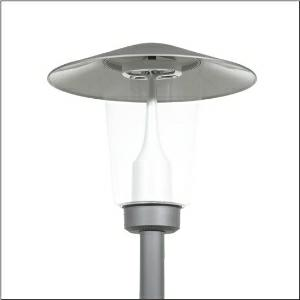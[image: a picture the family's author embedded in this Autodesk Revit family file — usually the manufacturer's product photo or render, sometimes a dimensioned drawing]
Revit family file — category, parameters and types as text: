
# Revit family: pilzleuchte_iq___st1_2a_5xa5235mf14h_7035
name_source: partatom
category: Lighting Fixtures
units: mm (PartAtom-declared; Revit-internal decimal feet)

## family parameters
Cut with Voids When Loaded = No
Host = Face
Light Source = No
Part Type = Normal
Room Calculation Point = No
Round Connector Dimension = Use Diameter
Shared = No

## types (1)
- --- (1 x LED, 1550 lm, 11.8 W, 2700K)
    Apparent Load = 12 VA
    CIE Flux Codes = 24 61 93 98 100
    Color Rendering = 70
    Color Temperature = 2700K
    Default Elevation = 1800 mm
    Description = Mushroom Luminaire iQ, mast luminaire, Module 540 iQ-SR, primary light control with 3 zone facetted reflector, of plastic, silver coated, highly specular, structured, primary optical cover: cover, of PMMA, transparent, light distribution: ST1.2a, light emission: direct distribution, primary light characteristic: asymmetric, installation type: post-top, LED, High Power LED, rated luminous flux: 1.550lm, luminous efficacy: 131lm/W, light colour: 727, colour temperature: 2700K, control gear: iQ Street-Remote, control: pre-setting: logarithmic dimming characteristic, Street-Remote, Auto-Match, Temp-Guard, Lumen-Switch, Night-Set, Smart-Wire, Light-Fading, Desk-Remote (wireless, voltage-free reading and setting of iQ features in the workshop via application-optimized NFC function/RFID function), optimised constant luminous flux control (CLO 2.0), with terminal, 6-pole, max. 2.5mm², mains connection: 230..240V, AC, 50/60Hz, start of lifetime: 12W, end of service life: 12W, reduction: 6W, luminaire housing, upper part, of glass-fibre reinforced polyester, coated, Siteco® metallic grey (DB 702S), diameter: 650mm, height: 586mm, spigot size: d x l = 76 x 70mm (post-top) | with reducer (optional accessory) 60 x 70mm, mounting height: 3..5m, post-top mast mounting element, of diecast aluminium, coated, Siteco® metallic grey (DB 702S), Module 540 iQ-SR, traffic white (RAL 9016), equipment: standard, protection rating (complete): IP65, insulation class (complete): insulation class II (safety insulation), certification: CE, ENEC, VDE, packaging unit: 1 piece

Light Distribution: ST1.2a
    Height = 586 mm
    Lamp = 1 x LED
    Lamp Light Flux = 1550 lm
    Lamp Power = 11.8 W
    Lamp count = 1
    Length = 650 mm
    Luminous efficacy = 131 lm/W
    Manufacturer = Siteco
    ModVariant = No
    Model = 5XA5235MF14H
    Number of Poles = 1
    OnlyDefault = Yes
    Power Factor = 1
    Product Name = Pilzleuchte iQ | ST1.2a
    Product group = mast luminaire | pylon top
    ProductGroupID = 6100
    Protection Class = Protection class II
    Protection Degree = IP 65
    RLX_Detail_Level = 1
    RLX_Emergency_Light_Flux = 0 lm
    RLX_Emergency_Type = 0
    RLX_Emergency_Type_DB = No
    RlxData = <blob elided: 123557 chars, md5=e10f4579>
    Socket = socket
    Standby Power = 0 W
    System Light Flux = 1550 lm
    System Power = 12 W
    Type Comments = factory setting: luminous flux: 100 % | dim-lin: 254 | 472 mA
    Type Image = l_1006077.jpg
    URL = http://relux.com
    VarID = @adj_152931
    Voltage = 0 V
    Weight = 0.00 kg
    Width = 0 mm  [stored 0 ft]

note: [stored X ft] marks values corroborated as IEEE doubles in the binary element streams (Revit-internal decimal feet)

## geometry (parser evidence)
native form markers: Blend x4, Sweep x11
no freeform markers — native parametric forms only
